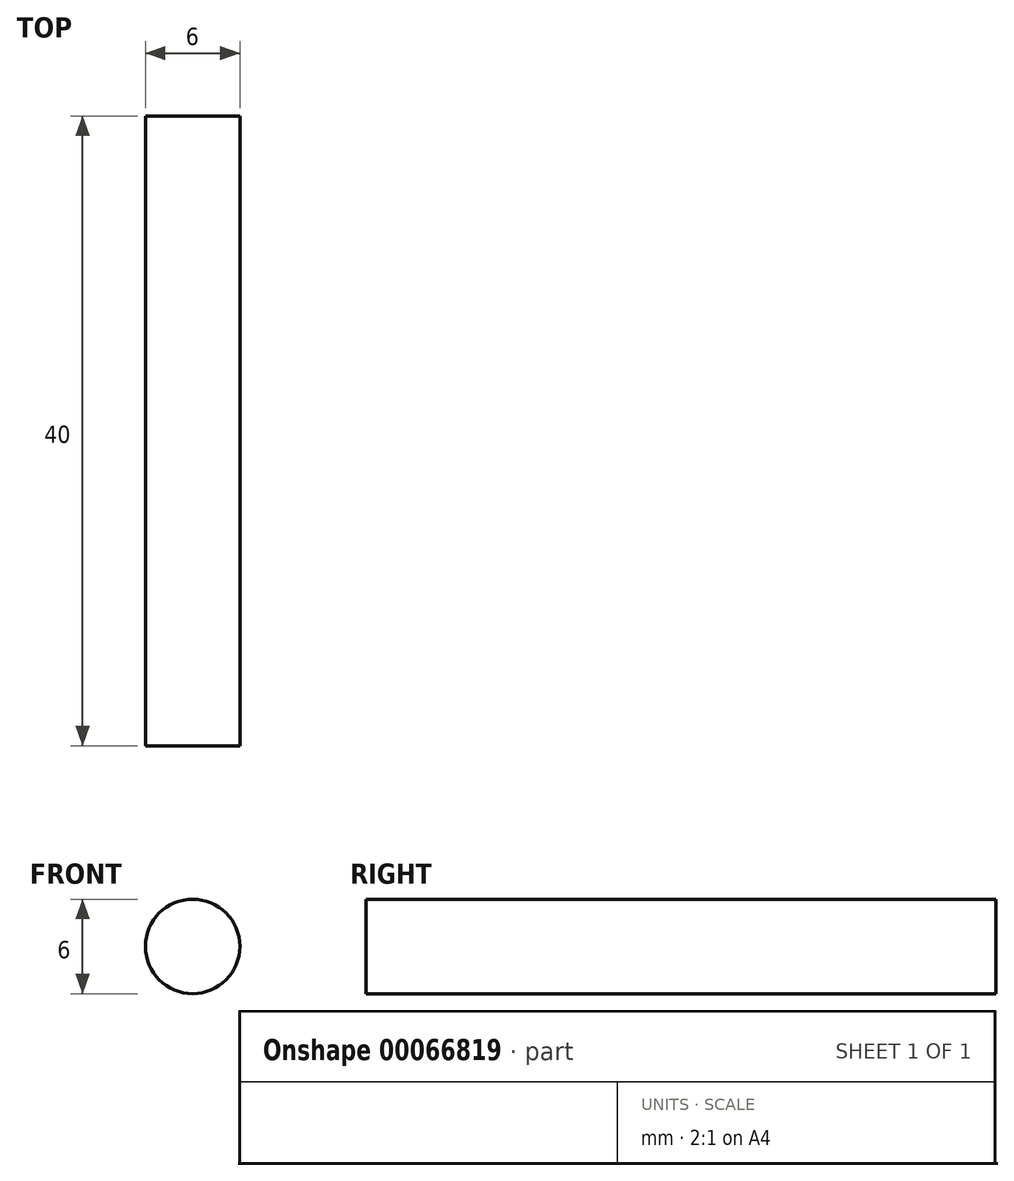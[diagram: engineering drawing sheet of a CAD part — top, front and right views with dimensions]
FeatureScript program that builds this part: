
annotation { "Feature Type Name" : "Feature", "Feature Type Description" : "" }
export const myFeature = defineFeature(function(context is Context, id is Id, definition is map)
    precondition{}
    {
        {
            var Q0;
            Q0=qCreatedBy(makeId("Front.planeOp"),FACE);
            var sketch = newSketch(context, id + "F0", { "sketchPlane" : qUnion([Q0])});
            skCircle(sketch, "E0", {"center": v(0, 0) * mm, "radius": 3 * mm});
            skSolve(sketch);
        }
        {
            var Q0;
            Q0=makeQuery(id+"F0.imprint","IMPRINT",FACE,{"disambiguationData":[TD([[makeQuery(id+"F0.imprint","IMPRINT",EDGE,{"derivedFrom":sQuery(id+"F0.wireOp",EDGE,"E0")}),1.0]])]});
            extrude(context, id + "F1", {"entities" : qUnion([Q0]), "depth" : 40 * mm});
        }
    });
